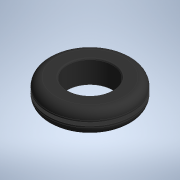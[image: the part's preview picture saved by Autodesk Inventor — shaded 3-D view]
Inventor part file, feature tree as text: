
AUTODESK INVENTOR PART (.ipt)
format: ipt  version: 2020 (Build 240168000, 168)  size: 123,392 bytes
history: native  units: mm (DEFAULTED — no unit token found)
features: fillet x1
ambient origin geometry x8: Origin, YZ Plane, XZ Plane, XY Plane, X Axis, Y Axis, Z Axis, Center Point
bodies: Solid1 (feature_tree)
feature tree (1):
  fillet  "Fillet1"  [1 undecoded]
note: 1 required parameter value undecoded (feature->parameter linkage not recoverable at this tier; creation-order binding heuristic only, values carry confidence <= 0.55)
